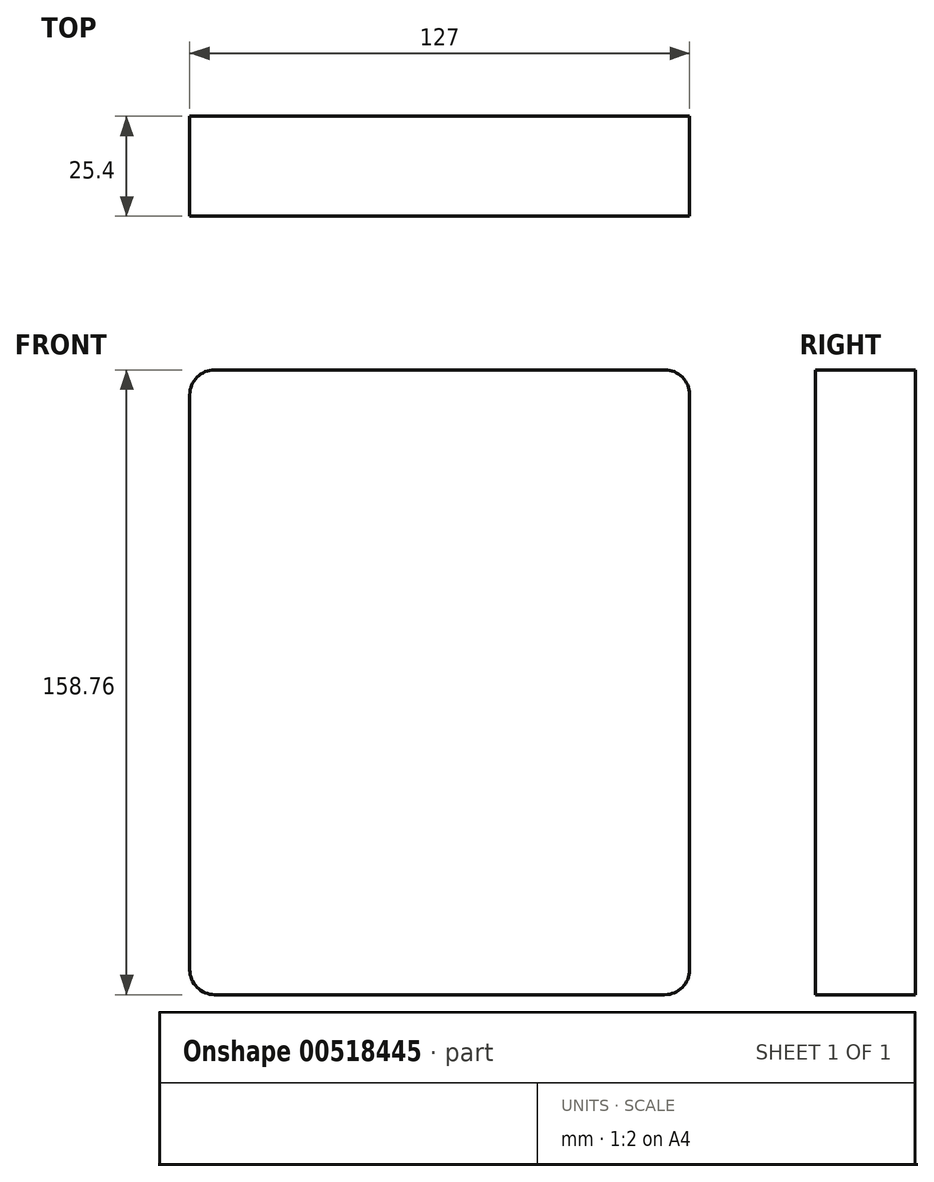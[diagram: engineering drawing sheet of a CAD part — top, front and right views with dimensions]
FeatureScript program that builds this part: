
annotation { "Feature Type Name" : "Feature", "Feature Type Description" : "" }
export const myFeature = defineFeature(function(context is Context, id is Id, definition is map)
    precondition{}
    {
        {
            var Q0;
            Q0=qCreatedBy(makeId("Front.planeOp"),FACE);
            var sketch = newSketch(context, id + "F0", { "sketchPlane" : qUnion([Q0])});
            skLineSegment(sketch, "E0.bottom", {"start": v(-57.15, -79.38) * mm, "end": v(57.15, -79.38) * mm});
            skLineSegment(sketch, "E0.top", {"start": v(-57.15, 79.38) * mm, "end": v(57.15, 79.38) * mm});
            skLineSegment(sketch, "E0.left", {"start": v(-63.5, -73.03) * mm, "end": v(-63.5, 73.03) * mm});
            skLineSegment(sketch, "E0.right", {"start": v(63.5, -73.03) * mm, "end": v(63.5, 73.03) * mm});
            skPoint(sketch, "E0.middle", {"position": v(0, 0) * mm});
            skPoint(sketch, "E1.visualSharp", {"position": v(63.5, 79.38) * mm});
            skArc(sketch, "E1.filletArc", {"start": v(63.5, 73.03) * mm, "mid": v(61.64, 77.52) * mm, "end": v(57.15, 79.38) * mm});
            skPoint(sketch, "E2.visualSharp", {"position": v(-63.5, 79.38) * mm});
            skArc(sketch, "E2.filletArc", {"start": v(-57.15, 79.38) * mm, "mid": v(-61.64, 77.52) * mm, "end": v(-63.5, 73.03) * mm});
            skPoint(sketch, "E3.visualSharp", {"position": v(-63.5, -79.38) * mm});
            skArc(sketch, "E3.filletArc", {"start": v(-63.5, -73.03) * mm, "mid": v(-61.64, -77.52) * mm, "end": v(-57.15, -79.38) * mm});
            skPoint(sketch, "E4.visualSharp", {"position": v(63.5, -79.38) * mm});
            skArc(sketch, "E4.filletArc", {"start": v(57.15, -79.38) * mm, "mid": v(61.64, -77.52) * mm, "end": v(63.5, -73.03) * mm});
            skSolve(sketch);
        }
        {
            var Q0;
            Q0=makeQuery(id+"F0.imprint","IMPRINT",FACE,{"disambiguationData":[TD([[makeQuery(id+"F0.imprint","IMPRINT",EDGE,{"derivedFrom":sQuery(id+"F0.wireOp",EDGE,"E0.bottom")}),1.0]])]});
            extrude(context, id + "F1", {"entities" : qUnion([Q0]), "depth" : 25.4 * mm, "offsetDistance" : 25.4 * mm});
        }
    });
